# Revit family: VTi.951.I_959.I_Фитинг_пресс-угольник_Нерж_VALTEC
name_source: partatom
category: Соединительные детали трубопроводов
units: mm (PartAtom-declared; Revit-internal decimal feet)

## family parameters
Всегда вертикально = Да
На основе рабочей плоскости = Нет
Общий = Нет
При загрузке вырезать с полостями = Нет
Размер круглого соединителя = Использовать диаметр
Тип детали = Отвод

## types (18) — shared parameters
ADSK_Единица измерения = шт.
ADSK_Количество = 1
ADSK_Материал = Сталь, нержавеющая - VALTEC
LT = VTi.951.I_959.I_Фитинг_пресс-угольник_Нерж_VALTEC
zero-valued in all types: Отметка по умолчанию

## type names (no varying parameters)
- Фитинг из нержавеющей стали - пресс-угольник 90° 12 мм
- Фитинг из нержавеющей стали - пресс-угольник 90° 15 мм
- Фитинг из нержавеющей стали - пресс-угольник 90° 18 мм
- Фитинг из нержавеющей стали - пресс-угольник 90° 22 мм
- Фитинг из нержавеющей стали - пресс-угольник 90° 28 мм
- Фитинг из нержавеющей стали - пресс-угольник 90° 35 мм
- Фитинг из нержавеющей стали - пресс-угольник 90° 42 мм
- Фитинг из нержавеющей стали - пресс-угольник 90° 54 мм
- Фитинг из нержавеющей стали - пресс-угольник 90° 76 мм
- Фитинг из нержавеющей стали - пресс-угольник 45° 12 мм
- Фитинг из нержавеющей стали - пресс-угольник 45° 15 мм
- Фитинг из нержавеющей стали - пресс-угольник 45° 18 мм
- Фитинг из нержавеющей стали - пресс-угольник 45° 22 мм
- Фитинг из нержавеющей стали - пресс-угольник 45° 28 мм
- Фитинг из нержавеющей стали - пресс-угольник 45° 35 мм
- Фитинг из нержавеющей стали - пресс-угольник 45° 42 мм
- Фитинг из нержавеющей стали - пресс-угольник 45° 54 мм
- Фитинг из нержавеющей стали - пресс-угольник 45° 76 мм
